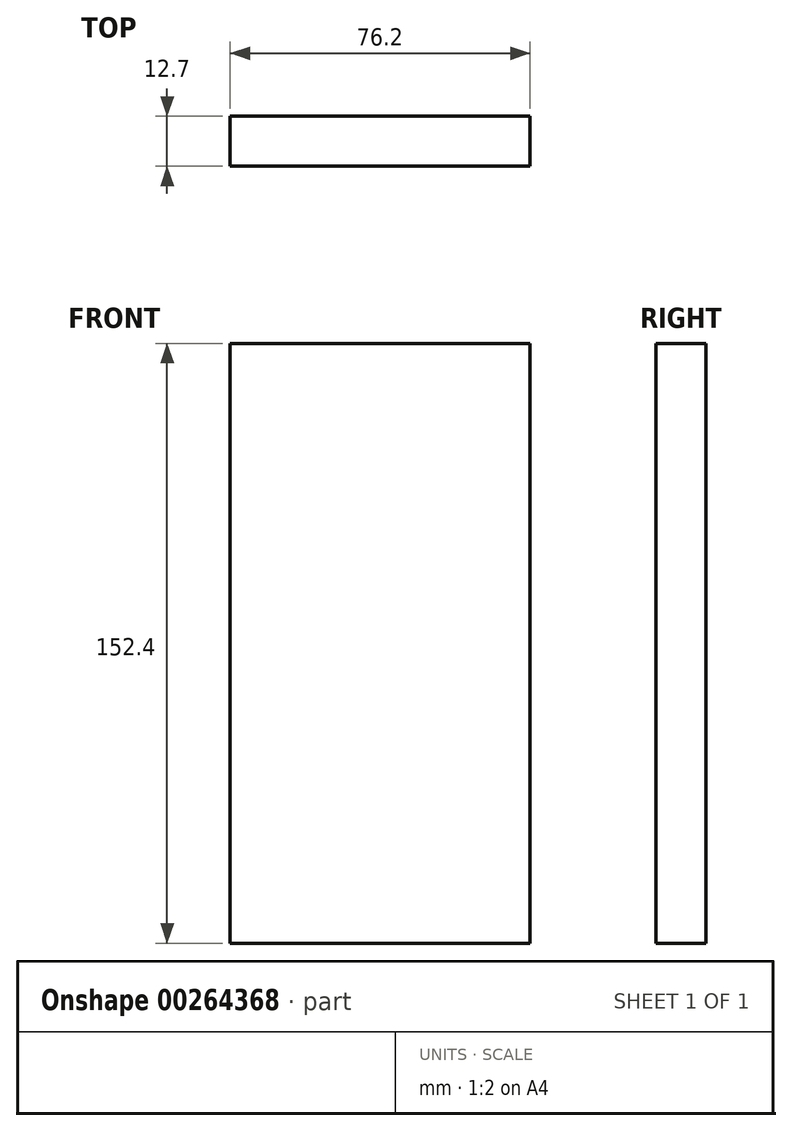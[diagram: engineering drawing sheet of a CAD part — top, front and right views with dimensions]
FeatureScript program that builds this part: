
annotation { "Feature Type Name" : "Feature", "Feature Type Description" : "" }
export const myFeature = defineFeature(function(context is Context, id is Id, definition is map)
    precondition{}
    {
        {
            var Q0;
            Q0=qCreatedBy(makeId("Front.planeOp"),FACE);
            var sketch = newSketch(context, id + "F0", { "sketchPlane" : qUnion([Q0])});
            skLineSegment(sketch, "E0.bottom", {"start": v(-11.23, 69.45) * mm, "end": v(-49.33, 69.45) * mm});
            skLineSegment(sketch, "E0.top", {"start": v(-11.23, -6.75) * mm, "end": v(-49.33, -6.75) * mm});
            skLineSegment(sketch, "E0.left", {"start": v(-11.23, 69.45) * mm, "end": v(-11.23, -6.75) * mm});
            skLineSegment(sketch, "E0.right", {"start": v(-49.33, 69.45) * mm, "end": v(-49.33, -6.75) * mm});
            skPoint(sketch, "E0.middle", {"position": v(-30.28, 31.35) * mm});
            skLineSegment(sketch, "E1.bottom", {"start": v(13.4, 62.58) * mm, "end": v(51.5, 62.58) * mm});
            skLineSegment(sketch, "E1.top", {"start": v(13.4, -13.62) * mm, "end": v(51.5, -13.62) * mm});
            skLineSegment(sketch, "E1.left", {"start": v(13.4, 62.58) * mm, "end": v(13.4, -13.62) * mm});
            skLineSegment(sketch, "E1.right", {"start": v(51.5, 62.58) * mm, "end": v(51.5, -13.62) * mm});
            skPoint(sketch, "E1.middle", {"position": v(32.45, 24.48) * mm});
            skSolve(sketch);
        }
        {
            var Q0;
            Q0=qCreatedBy(makeId("Front.planeOp"),FACE);
            var sketch = newSketch(context, id + "F1", { "sketchPlane" : qUnion([Q0])});
            skLineSegment(sketch, "E2.bottom", {"start": v(38.1, 76.2) * mm, "end": v(-38.1, 76.2) * mm});
            skLineSegment(sketch, "E2.top", {"start": v(38.1, -76.2) * mm, "end": v(-38.1, -76.2) * mm});
            skLineSegment(sketch, "E2.left", {"start": v(38.1, 76.2) * mm, "end": v(38.1, -76.2) * mm});
            skLineSegment(sketch, "E2.right", {"start": v(-38.1, 76.2) * mm, "end": v(-38.1, -76.2) * mm});
            skPoint(sketch, "E2.middle", {"position": v(0, 0) * mm});
            skSolve(sketch);
        }
        {
            var Q0;
            Q0=makeQuery(id+"F1.imprint","IMPRINT",FACE,{"disambiguationData":[TD([[makeQuery(id+"F1.imprint","IMPRINT",EDGE,{"derivedFrom":sQuery(id+"F1.wireOp",EDGE,"E2.bottom")}),1.0]])]});
            extrude(context, id + "F2", {"entities" : qUnion([Q0]), "depth" : 12.7 * mm});
        }
    });
